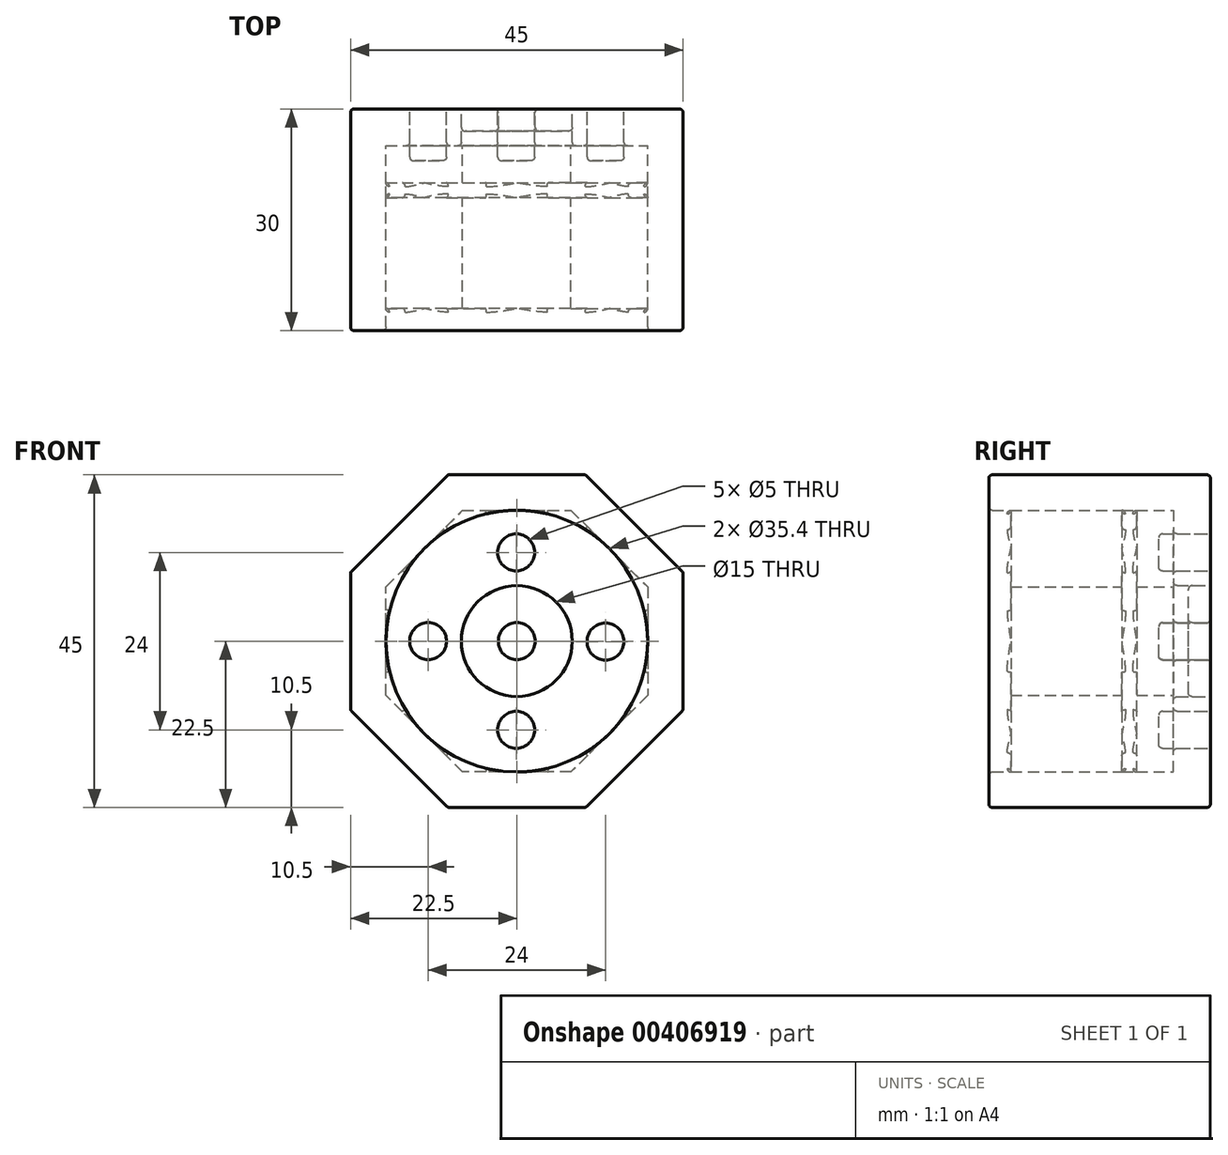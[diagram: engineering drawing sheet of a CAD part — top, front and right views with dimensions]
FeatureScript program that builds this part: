
annotation { "Feature Type Name" : "Feature", "Feature Type Description" : "" }
export const myFeature = defineFeature(function(context is Context, id is Id, definition is map)
    precondition{}
    {
        {
            var Q0;
            Q0=qCreatedBy(makeId("Front.planeOp"),FACE);
            var sketch = newSketch(context, id + "F0", { "sketchPlane" : qUnion([Q0])});
            skCircle(sketch, "E0.cCircle", {"center": v(0, 0) * mm, "radius": 17.7 * mm, "construction": true});
            skLineSegment(sketch, "E0.0", {"start": v(17.7, 7.33) * mm, "end": v(17.7, -7.33) * mm});
            skLineSegment(sketch, "E0.1", {"start": v(17.7, -7.33) * mm, "end": v(7.33, -17.7) * mm});
            skLineSegment(sketch, "E0.2", {"start": v(7.33, -17.7) * mm, "end": v(-7.33, -17.7) * mm});
            skLineSegment(sketch, "E0.3", {"start": v(-7.33, -17.7) * mm, "end": v(-17.7, -7.33) * mm});
            skLineSegment(sketch, "E0.4", {"start": v(-17.7, -7.33) * mm, "end": v(-17.7, 7.33) * mm});
            skLineSegment(sketch, "E0.5", {"start": v(-17.7, 7.33) * mm, "end": v(-7.33, 17.7) * mm});
            skLineSegment(sketch, "E0.6", {"start": v(-7.33, 17.7) * mm, "end": v(7.33, 17.7) * mm});
            skLineSegment(sketch, "E0.7", {"start": v(7.33, 17.7) * mm, "end": v(17.7, 7.33) * mm});
            skPoint(sketch, "E0.0.midPoint", {"position": v(17.7, 0) * mm});
            skCircle(sketch, "E1.cCircle", {"center": v(0, 0) * mm, "radius": 22.5 * mm, "construction": true});
            skLineSegment(sketch, "E1.0", {"start": v(9.32, 22.5) * mm, "end": v(22.5, 9.32) * mm});
            skLineSegment(sketch, "E1.1", {"start": v(22.5, 9.32) * mm, "end": v(22.5, -9.32) * mm});
            skLineSegment(sketch, "E1.2", {"start": v(22.5, -9.32) * mm, "end": v(9.32, -22.5) * mm});
            skLineSegment(sketch, "E1.3", {"start": v(9.32, -22.5) * mm, "end": v(-9.32, -22.5) * mm});
            skLineSegment(sketch, "E1.4", {"start": v(-9.32, -22.5) * mm, "end": v(-22.5, -9.32) * mm});
            skLineSegment(sketch, "E1.5", {"start": v(-22.5, -9.32) * mm, "end": v(-22.5, 9.32) * mm});
            skLineSegment(sketch, "E1.6", {"start": v(-22.5, 9.32) * mm, "end": v(-9.32, 22.5) * mm});
            skLineSegment(sketch, "E1.7", {"start": v(-9.32, 22.5) * mm, "end": v(9.32, 22.5) * mm});
            skPoint(sketch, "E1.0.midPoint", {"position": v(15.9, 15.9) * mm});
            skCircle(sketch, "E2", {"center": v(0, 0) * mm, "radius": 2.5 * mm});
            skCircle(sketch, "E3", {"center": v(0, 0) * mm, "radius": 7.5 * mm});
            skCircle(sketch, "E4", {"center": v(-12, 0) * mm, "radius": 2.5 * mm});
            skCircle(sketch, "E5", {"center": v(-0.08, 12) * mm, "radius": 2.5 * mm});
            skCircle(sketch, "E6", {"center": v(12, -0.06) * mm, "radius": 2.5 * mm});
            skCircle(sketch, "E7", {"center": v(-0.08, -12) * mm, "radius": 2.5 * mm});
            skSolve(sketch);
        }
        {
            var Q0;
            Q0=makeQuery(id+"F0.imprint","IMPRINT",FACE,{"disambiguationData":[TD([[makeQuery(id+"F0.imprint","IMPRINT",EDGE,{"derivedFrom":sQuery(id+"F0.wireOp",EDGE,"E2")}),-1.0]])]});
            extrude(context, id + "F1", {"entities" : qUnion([Q0]), "depth" : 3 * mm});
        }
        {
            var Q0;
            Q0=makeQuery(id+"F0.imprint","IMPRINT",FACE,{"disambiguationData":[TD([[makeQuery(id+"F0.imprint","IMPRINT",EDGE,{"derivedFrom":sQuery(id+"F0.wireOp",EDGE,"E4")}),1.0]])]});
            var Q1;
            Q1=makeQuery(id+"F0.imprint","IMPRINT",FACE,{"disambiguationData":[TD([[makeQuery(id+"F0.imprint","IMPRINT",EDGE,{"derivedFrom":sQuery(id+"F0.wireOp",EDGE,"E5")}),1.0]])]});
            var Q2;
            Q2=makeQuery(id+"F0.imprint","IMPRINT",FACE,{"disambiguationData":[TD([[makeQuery(id+"F0.imprint","IMPRINT",EDGE,{"derivedFrom":sQuery(id+"F0.wireOp",EDGE,"E6")}),1.0]])]});
            var Q3;
            Q3=makeQuery(id+"F0.imprint","IMPRINT",FACE,{"disambiguationData":[TD([[makeQuery(id+"F0.imprint","IMPRINT",EDGE,{"derivedFrom":sQuery(id+"F0.wireOp",EDGE,"E7")}),1.0]])]});
            extrude(context, id + "F2", {"entities" : qUnion([Q0, Q1, Q2, Q3]), "depth" : 7 * mm});
        }
        {
            var Q0;
            Q0=makeQuery(id+"F0.imprint","IMPRINT",FACE,{"disambiguationData":[TD([[makeQuery(id+"F0.imprint","IMPRINT",EDGE,{"derivedFrom":sQuery(id+"F0.wireOp",EDGE,"E0.0")}),-1.0]])]});
            extrude(context, id + "F3", {"entities" : qUnion([Q0]), "depth" : 5 * mm});
        }
        {
            var Q0;
            Q0=makeQuery(id+"F0.imprint","IMPRINT",FACE,{"disambiguationData":[TD([[makeQuery(id+"F0.imprint","IMPRINT",EDGE,{"derivedFrom":sQuery(id+"F0.wireOp",EDGE,"E0.0")}),1.0]])]});
            extrude(context, id + "F4", {"entities" : qUnion([Q0]), "operationType" : NewBodyOperationType.ADD, "depth" : 10 * mm});
        }
        {
            var Q0;
            Q0=makeQuery(id+"F4.opExtrude","CAP_FACE",FACE,{"disambiguationData":[OSD([sQuery(id+"F0.wireOp",EDGE,"E0.0"),sQuery(id+"F0.wireOp",EDGE,"E0.1"),sQuery(id+"F0.wireOp",EDGE,"E0.2"),sQuery(id+"F0.wireOp",EDGE,"E0.3"),sQuery(id+"F0.wireOp",EDGE,"E0.4"),sQuery(id+"F0.wireOp",EDGE,"E0.5"),sQuery(id+"F0.wireOp",EDGE,"E0.6"),sQuery(id+"F0.wireOp",EDGE,"E0.7"),sQuery(id+"F0.wireOp",EDGE,"E1.0"),sQuery(id+"F0.wireOp",EDGE,"E1.1"),sQuery(id+"F0.wireOp",EDGE,"E1.2"),sQuery(id+"F0.wireOp",EDGE,"E1.3"),sQuery(id+"F0.wireOp",EDGE,"E1.4"),sQuery(id+"F0.wireOp",EDGE,"E1.5"),sQuery(id+"F0.wireOp",EDGE,"E1.6"),sQuery(id+"F0.wireOp",EDGE,"E1.7")])],"isStart":false});
            var sketch = newSketch(context, id + "F5", { "sketchPlane" : qUnion([Q0])});
            skCircle(sketch, "E8", {"center": v(0, 0) * mm, "radius": 17.7 * mm});
            skSolve(sketch);
        }
        {
            var Q0;
            {var subQ0=sQuery(id+"F5.wireOp",EDGE,"E8");var subQ1=makeQuery(id+"F4.opExtrude","CAP_EDGE",EDGE,{"disambiguationData":[OSD([sQuery(id+"F0.wireOp",EDGE,"E0.4")])],"isStart":false});var subQ2=makeQuery(id+"F5.imprint","INTERSECT",VERTEX,{"derivedFrom":[subQ1,subQ0]});Q0=makeQuery(id+"F5.imprint","IMPRINT",FACE,{"disambiguationData":[TD([[makeQuery(id+"F5.imprint","IMPRINT",EDGE,{"disambiguationData":[TD([[subQ2,-1.0]])],"derivedFrom":subQ0}),-1.0]])]});}
            var Q1;
            {var subQ0=sQuery(id+"F5.wireOp",EDGE,"E8");var subQ1=makeQuery(id+"F4.opExtrude","CAP_EDGE",EDGE,{"disambiguationData":[OSD([sQuery(id+"F0.wireOp",EDGE,"E0.5")])],"isStart":false});var subQ2=makeQuery(id+"F5.imprint","INTERSECT",VERTEX,{"derivedFrom":[subQ1,subQ0]});Q1=makeQuery(id+"F5.imprint","IMPRINT",FACE,{"disambiguationData":[TD([[makeQuery(id+"F5.imprint","IMPRINT",EDGE,{"disambiguationData":[TD([[subQ2,-1.0]])],"derivedFrom":subQ0}),-1.0]])]});}
            var Q2;
            {var subQ0=sQuery(id+"F5.wireOp",EDGE,"E8");var subQ1=makeQuery(id+"F4.opExtrude","CAP_EDGE",EDGE,{"disambiguationData":[OSD([sQuery(id+"F0.wireOp",EDGE,"E0.6")])],"isStart":false});var subQ2=makeQuery(id+"F5.imprint","INTERSECT",VERTEX,{"derivedFrom":[subQ1,subQ0]});Q2=makeQuery(id+"F5.imprint","IMPRINT",FACE,{"disambiguationData":[TD([[makeQuery(id+"F5.imprint","IMPRINT",EDGE,{"disambiguationData":[TD([[subQ2,-1.0]])],"derivedFrom":subQ0}),-1.0]])]});}
            var Q3;
            {var subQ0=sQuery(id+"F5.wireOp",EDGE,"E8");var subQ1=makeQuery(id+"F4.opExtrude","CAP_EDGE",EDGE,{"disambiguationData":[OSD([sQuery(id+"F0.wireOp",EDGE,"E0.7")])],"isStart":false});var subQ2=makeQuery(id+"F5.imprint","INTERSECT",VERTEX,{"derivedFrom":[subQ1,subQ0]});Q3=makeQuery(id+"F5.imprint","IMPRINT",FACE,{"disambiguationData":[TD([[makeQuery(id+"F5.imprint","IMPRINT",EDGE,{"disambiguationData":[TD([[subQ2,-1.0]])],"derivedFrom":subQ0}),-1.0]])]});}
            var Q4;
            {var subQ0=sQuery(id+"F5.wireOp",EDGE,"E8");var subQ1=makeQuery(id+"F4.opExtrude","CAP_EDGE",EDGE,{"disambiguationData":[OSD([sQuery(id+"F0.wireOp",EDGE,"E0.7")])],"isStart":false});var subQ2=makeQuery(id+"F5.imprint","INTERSECT",VERTEX,{"derivedFrom":[subQ1,subQ0]});Q4=makeQuery(id+"F5.imprint","IMPRINT",FACE,{"disambiguationData":[TD([[makeQuery(id+"F5.imprint","IMPRINT",EDGE,{"disambiguationData":[TD([[subQ2,1.0]])],"derivedFrom":subQ0}),-1.0]])]});}
            var Q5;
            {var subQ0=sQuery(id+"F5.wireOp",EDGE,"E8");var subQ1=makeQuery(id+"F4.opExtrude","CAP_EDGE",EDGE,{"disambiguationData":[OSD([sQuery(id+"F0.wireOp",EDGE,"E0.0")])],"isStart":false});var subQ2=makeQuery(id+"F5.imprint","INTERSECT",VERTEX,{"derivedFrom":[subQ1,subQ0]});Q5=makeQuery(id+"F5.imprint","IMPRINT",FACE,{"disambiguationData":[TD([[makeQuery(id+"F5.imprint","IMPRINT",EDGE,{"disambiguationData":[TD([[subQ2,1.0]])],"derivedFrom":subQ0}),-1.0]])]});}
            var Q6;
            {var subQ0=sQuery(id+"F5.wireOp",EDGE,"E8");var subQ1=makeQuery(id+"F4.opExtrude","CAP_EDGE",EDGE,{"disambiguationData":[OSD([sQuery(id+"F0.wireOp",EDGE,"E0.2")])],"isStart":false});var subQ2=makeQuery(id+"F5.imprint","INTERSECT",VERTEX,{"derivedFrom":[subQ1,subQ0]});Q6=makeQuery(id+"F5.imprint","IMPRINT",FACE,{"disambiguationData":[TD([[makeQuery(id+"F5.imprint","IMPRINT",EDGE,{"disambiguationData":[TD([[subQ2,-1.0]])],"derivedFrom":subQ0}),-1.0]])]});}
            var Q7;
            {var subQ0=sQuery(id+"F5.wireOp",EDGE,"E8");var subQ1=makeQuery(id+"F4.opExtrude","CAP_EDGE",EDGE,{"disambiguationData":[OSD([sQuery(id+"F0.wireOp",EDGE,"E0.3")])],"isStart":false});var subQ2=makeQuery(id+"F5.imprint","INTERSECT",VERTEX,{"derivedFrom":[subQ1,subQ0]});Q7=makeQuery(id+"F5.imprint","IMPRINT",FACE,{"disambiguationData":[TD([[makeQuery(id+"F5.imprint","IMPRINT",EDGE,{"disambiguationData":[TD([[subQ2,-1.0]])],"derivedFrom":subQ0}),-1.0]])]});}
            var Q8;
            Q8=makeQuery(id+"F5.imprint","IMPRINT",FACE,{"disambiguationData":[TD([[makeQuery(id+"F5.imprint","IMPRINT",EDGE,{"derivedFrom":makeQuery(id+"F4.opExtrude","CAP_EDGE",EDGE,{"disambiguationData":[OSD([sQuery(id+"F0.wireOp",EDGE,"E1.0")])],"isStart":false})}),-1.0]])]});
            extrude(context, id + "F6", {"entities" : qUnion([Q0, Q1, Q2, Q3, Q4, Q5, Q6, Q7, Q8]), "operationType" : NewBodyOperationType.ADD, "depth" : 2 * mm});
        }
        {
            var Q0;
            Q0=makeQuery(id+"F6.opExtrude","CAP_FACE",FACE,{"disambiguationData":[OSD([sQuery(id+"F0.wireOp",EDGE,"E1.0"),sQuery(id+"F0.wireOp",EDGE,"E1.1"),sQuery(id+"F0.wireOp",EDGE,"E1.2"),sQuery(id+"F0.wireOp",EDGE,"E1.3"),sQuery(id+"F0.wireOp",EDGE,"E1.4"),sQuery(id+"F0.wireOp",EDGE,"E1.5"),sQuery(id+"F0.wireOp",EDGE,"E1.6"),sQuery(id+"F0.wireOp",EDGE,"E1.7"),sQuery(id+"F5.wireOp",EDGE,"E8")])],"isStart":false});
            var sketch = newSketch(context, id + "F7", { "sketchPlane" : qUnion([Q0])});
            skCircle(sketch, "E9.cCircle", {"center": v(0, 0) * mm, "radius": 17.7 * mm, "construction": true});
            skLineSegment(sketch, "E10.0", {"start": v(-17.7, -7.33) * mm, "end": v(-17.7, 7.33) * mm});
            skLineSegment(sketch, "E10.1", {"start": v(-17.7, 7.33) * mm, "end": v(-7.33, 17.7) * mm});
            skLineSegment(sketch, "E10.2", {"start": v(-7.33, 17.7) * mm, "end": v(7.33, 17.7) * mm});
            skLineSegment(sketch, "E10.3", {"start": v(7.33, 17.7) * mm, "end": v(17.7, 7.33) * mm});
            skLineSegment(sketch, "E10.4", {"start": v(17.7, 7.33) * mm, "end": v(17.7, -7.33) * mm});
            skLineSegment(sketch, "E10.5", {"start": v(17.7, -7.33) * mm, "end": v(7.33, -17.7) * mm});
            skLineSegment(sketch, "E10.6", {"start": v(7.33, -17.7) * mm, "end": v(-7.33, -17.7) * mm});
            skLineSegment(sketch, "E10.7", {"start": v(-7.33, -17.7) * mm, "end": v(-17.7, -7.33) * mm});
            skPoint(sketch, "E10.0.midPoint", {"position": v(-17.7, 0) * mm});
            skSolve(sketch);
        }
        {
            var Q0;
            Q0=makeQuery(id+"F7.imprint","IMPRINT",FACE,{"disambiguationData":[TD([[makeQuery(id+"F7.imprint","IMPRINT",EDGE,{"derivedFrom":makeQuery(id+"F6.opExtrude","CAP_EDGE",EDGE,{"disambiguationData":[OSD([sQuery(id+"F0.wireOp",EDGE,"E1.0")])],"isStart":false})}),-1.0]])]});
            extrude(context, id + "F8", {"entities" : qUnion([Q0]), "operationType" : NewBodyOperationType.ADD, "depth" : 15 * mm});
        }
        {
            var Q0;
            Q0=makeQuery(id+"F8.opExtrude","CAP_FACE",FACE,{"disambiguationData":[OSD([sQuery(id+"F0.wireOp",EDGE,"E1.0"),sQuery(id+"F0.wireOp",EDGE,"E1.1"),sQuery(id+"F0.wireOp",EDGE,"E1.2"),sQuery(id+"F0.wireOp",EDGE,"E1.3"),sQuery(id+"F0.wireOp",EDGE,"E1.4"),sQuery(id+"F0.wireOp",EDGE,"E1.5"),sQuery(id+"F0.wireOp",EDGE,"E1.6"),sQuery(id+"F0.wireOp",EDGE,"E1.7"),sQuery(id+"F7.wireOp",EDGE,"E9.0"),sQuery(id+"F7.wireOp",EDGE,"E9.1"),sQuery(id+"F7.wireOp",EDGE,"E9.2"),sQuery(id+"F7.wireOp",EDGE,"E9.3"),sQuery(id+"F7.wireOp",EDGE,"E9.4"),sQuery(id+"F7.wireOp",EDGE,"E9.5"),sQuery(id+"F7.wireOp",EDGE,"E9.6"),sQuery(id+"F7.wireOp",EDGE,"E9.7"),sQuery(id+"F7.wireOp",EDGE,"E9.8")])],"isStart":false});
            var sketch = newSketch(context, id + "F9", { "sketchPlane" : qUnion([Q0])});
            skCircle(sketch, "E11", {"center": v(0, 0) * mm, "radius": 17.7 * mm});
            skSolve(sketch);
        }
        {
            var Q0;
            {var subQ0=sQuery(id+"F9.wireOp",EDGE,"E11");var subQ1=makeQuery(id+"F8.opExtrude","CAP_EDGE",EDGE,{"disambiguationData":[OSD([sQuery(id+"F7.wireOp",EDGE,"E9.5")])],"isStart":false});var subQ2=makeQuery(id+"F9.imprint","INTERSECT",VERTEX,{"derivedFrom":[subQ1,subQ0]});Q0=makeQuery(id+"F9.imprint","IMPRINT",FACE,{"disambiguationData":[TD([[makeQuery(id+"F9.imprint","IMPRINT",EDGE,{"disambiguationData":[TD([[subQ2,-1.0]])],"derivedFrom":subQ0}),-1.0]])]});}
            var Q1;
            {var subQ0=sQuery(id+"F9.wireOp",EDGE,"E11");var subQ1=makeQuery(id+"F8.opExtrude","CAP_EDGE",EDGE,{"disambiguationData":[OSD([sQuery(id+"F7.wireOp",EDGE,"E9.6")])],"isStart":false});var subQ2=makeQuery(id+"F9.imprint","INTERSECT",VERTEX,{"derivedFrom":[subQ1,subQ0]});Q1=makeQuery(id+"F9.imprint","IMPRINT",FACE,{"disambiguationData":[TD([[makeQuery(id+"F9.imprint","IMPRINT",EDGE,{"disambiguationData":[TD([[subQ2,-1.0]])],"derivedFrom":subQ0}),-1.0]])]});}
            var Q2;
            {var subQ0=sQuery(id+"F9.wireOp",EDGE,"E11");var subQ1=makeQuery(id+"F8.opExtrude","CAP_EDGE",EDGE,{"disambiguationData":[OSD([sQuery(id+"F7.wireOp",EDGE,"E9.7")])],"isStart":false});var subQ2=makeQuery(id+"F9.imprint","INTERSECT",VERTEX,{"derivedFrom":[subQ1,subQ0]});Q2=makeQuery(id+"F9.imprint","IMPRINT",FACE,{"disambiguationData":[TD([[makeQuery(id+"F9.imprint","IMPRINT",EDGE,{"disambiguationData":[TD([[subQ2,-1.0]])],"derivedFrom":subQ0}),-1.0]])]});}
            var Q3;
            {var subQ0=sQuery(id+"F9.wireOp",EDGE,"E11");var subQ1=makeQuery(id+"F8.opExtrude","CAP_EDGE",EDGE,{"disambiguationData":[OSD([sQuery(id+"F7.wireOp",EDGE,"E9.8")])],"isStart":false});var subQ2=makeQuery(id+"F9.imprint","INTERSECT",VERTEX,{"derivedFrom":[subQ1,subQ0]});Q3=makeQuery(id+"F9.imprint","IMPRINT",FACE,{"disambiguationData":[TD([[makeQuery(id+"F9.imprint","IMPRINT",EDGE,{"disambiguationData":[TD([[subQ2,-1.0]])],"derivedFrom":subQ0}),-1.0]])]});}
            var Q4;
            {var subQ0=sQuery(id+"F9.wireOp",EDGE,"E11");var subQ1=makeQuery(id+"F8.opExtrude","CAP_EDGE",EDGE,{"disambiguationData":[OSD([sQuery(id+"F7.wireOp",EDGE,"E9.0")])],"isStart":false});var subQ2=makeQuery(id+"F9.imprint","INTERSECT",VERTEX,{"derivedFrom":[subQ1,subQ0]});Q4=makeQuery(id+"F9.imprint","IMPRINT",FACE,{"disambiguationData":[TD([[makeQuery(id+"F9.imprint","IMPRINT",EDGE,{"disambiguationData":[TD([[subQ2,-1.0]])],"derivedFrom":subQ0}),-1.0]])]});}
            var Q5;
            {var subQ0=sQuery(id+"F9.wireOp",EDGE,"E11");var subQ1=makeQuery(id+"F8.opExtrude","CAP_EDGE",EDGE,{"disambiguationData":[OSD([sQuery(id+"F7.wireOp",EDGE,"E9.0")])],"isStart":false});var subQ2=makeQuery(id+"F9.imprint","INTERSECT",VERTEX,{"derivedFrom":[subQ1,subQ0]});Q5=makeQuery(id+"F9.imprint","IMPRINT",FACE,{"disambiguationData":[TD([[makeQuery(id+"F9.imprint","IMPRINT",EDGE,{"disambiguationData":[TD([[subQ2,1.0]])],"derivedFrom":subQ0}),-1.0]])]});}
            var Q6;
            {var subQ0=sQuery(id+"F9.wireOp",EDGE,"E11");var subQ1=makeQuery(id+"F8.opExtrude","CAP_EDGE",EDGE,{"disambiguationData":[OSD([sQuery(id+"F7.wireOp",EDGE,"E9.1")])],"isStart":false});var subQ2=makeQuery(id+"F9.imprint","INTERSECT",VERTEX,{"derivedFrom":[subQ1,subQ0]});Q6=makeQuery(id+"F9.imprint","IMPRINT",FACE,{"disambiguationData":[TD([[makeQuery(id+"F9.imprint","IMPRINT",EDGE,{"disambiguationData":[TD([[subQ2,1.0]])],"derivedFrom":subQ0}),-1.0]])]});}
            var Q7;
            {var subQ0=sQuery(id+"F9.wireOp",EDGE,"E11");var subQ1=makeQuery(id+"F8.opExtrude","CAP_EDGE",EDGE,{"disambiguationData":[OSD([sQuery(id+"F7.wireOp",EDGE,"E9.3")])],"isStart":false});var subQ2=makeQuery(id+"F9.imprint","INTERSECT",VERTEX,{"derivedFrom":[subQ1,subQ0]});Q7=makeQuery(id+"F9.imprint","IMPRINT",FACE,{"disambiguationData":[TD([[makeQuery(id+"F9.imprint","IMPRINT",EDGE,{"disambiguationData":[TD([[subQ2,-1.0]])],"derivedFrom":subQ0}),-1.0]])]});}
            var Q8;
            {var subQ0=sQuery(id+"F9.wireOp",EDGE,"E11");var subQ1=makeQuery(id+"F8.opExtrude","CAP_EDGE",EDGE,{"disambiguationData":[OSD([sQuery(id+"F7.wireOp",EDGE,"E9.4")])],"isStart":false});var subQ2=makeQuery(id+"F9.imprint","INTERSECT",VERTEX,{"derivedFrom":[subQ1,subQ0]});Q8=makeQuery(id+"F9.imprint","IMPRINT",FACE,{"disambiguationData":[TD([[makeQuery(id+"F9.imprint","IMPRINT",EDGE,{"disambiguationData":[TD([[subQ2,-1.0]])],"derivedFrom":subQ0}),-1.0]])]});}
            var Q9;
            Q9=makeQuery(id+"F9.imprint","IMPRINT",FACE,{"disambiguationData":[TD([[makeQuery(id+"F9.imprint","IMPRINT",EDGE,{"derivedFrom":makeQuery(id+"F8.opExtrude","CAP_EDGE",EDGE,{"disambiguationData":[OSD([sQuery(id+"F0.wireOp",EDGE,"E1.0")])],"isStart":false})}),-1.0]])]});
            extrude(context, id + "F10", {"entities" : qUnion([Q0, Q1, Q2, Q3, Q4, Q5, Q6, Q7, Q8, Q9]), "operationType" : NewBodyOperationType.ADD, "depth" : 3 * mm});
        }
        {
            var Q0;
            Q0=makeQuery(id+"F1.opExtrude","CAP_EDGE",EDGE,{"disambiguationData":[OSD([sQuery(id+"F0.wireOp",EDGE,"E2")])],"isStart":true});
            var Q1;
            Q1=makeQuery(id+"F4.opExtrude","CAP_EDGE",EDGE,{"disambiguationData":[OSD([sQuery(id+"F0.wireOp",EDGE,"E1.7")])],"isStart":true});
            var Q2;
            Q2=makeQuery(id+"F4.opExtrude","CAP_EDGE",EDGE,{"disambiguationData":[OSD([sQuery(id+"F0.wireOp",EDGE,"E1.6")])],"isStart":true});
            var Q3;
            Q3=makeQuery(id+"F4.opExtrude","CAP_EDGE",EDGE,{"disambiguationData":[OSD([sQuery(id+"F0.wireOp",EDGE,"E1.5")])],"isStart":true});
            var Q4;
            Q4=makeQuery(id+"F4.opExtrude","CAP_EDGE",EDGE,{"disambiguationData":[OSD([sQuery(id+"F0.wireOp",EDGE,"E1.4")])],"isStart":true});
            var Q5;
            Q5=makeQuery(id+"F4.opExtrude","CAP_EDGE",EDGE,{"disambiguationData":[OSD([sQuery(id+"F0.wireOp",EDGE,"E1.3")])],"isStart":true});
            var Q6;
            Q6=makeQuery(id+"F4.opExtrude","CAP_EDGE",EDGE,{"disambiguationData":[OSD([sQuery(id+"F0.wireOp",EDGE,"E1.2")])],"isStart":true});
            var Q7;
            Q7=makeQuery(id+"F4.opExtrude","CAP_EDGE",EDGE,{"disambiguationData":[OSD([sQuery(id+"F0.wireOp",EDGE,"E1.1")])],"isStart":true});
            var Q8;
            Q8=makeQuery(id+"F4.opExtrude","CAP_EDGE",EDGE,{"disambiguationData":[OSD([sQuery(id+"F0.wireOp",EDGE,"E1.0")])],"isStart":true});
            var Q9;
            {var subQ0=sQuery(id+"F0.wireOp",EDGE,"E1.6");Q9=makeQuery(id+"F10.boolean.opBoolean","MERGE",FACE,{"derivedFrom":[makeQuery(id+"F8.boolean.opBoolean","MERGE",FACE,{"derivedFrom":[makeQuery(id+"F6.boolean.opBoolean","MERGE",FACE,{"derivedFrom":[makeQuery(id+"F4.opExtrude","SWEPT_FACE",FACE,{"disambiguationData":[OSD([subQ0])]}),makeQuery(id+"F6.opExtrude","SWEPT_FACE",FACE,{"disambiguationData":[OSD([subQ0])]})]}),makeQuery(id+"F8.opExtrude","SWEPT_FACE",FACE,{"disambiguationData":[OSD([subQ0])]})]}),makeQuery(id+"F10.opExtrude","SWEPT_FACE",FACE,{"disambiguationData":[OSD([subQ0])]})]});}
            var Q10;
            {var subQ0=sQuery(id+"F0.wireOp",EDGE,"E1.5");Q10=makeQuery(id+"F10.boolean.opBoolean","MERGE",FACE,{"derivedFrom":[makeQuery(id+"F8.boolean.opBoolean","MERGE",FACE,{"derivedFrom":[makeQuery(id+"F6.boolean.opBoolean","MERGE",FACE,{"derivedFrom":[makeQuery(id+"F4.opExtrude","SWEPT_FACE",FACE,{"disambiguationData":[OSD([subQ0])]}),makeQuery(id+"F6.opExtrude","SWEPT_FACE",FACE,{"disambiguationData":[OSD([subQ0])]})]}),makeQuery(id+"F8.opExtrude","SWEPT_FACE",FACE,{"disambiguationData":[OSD([subQ0])]})]}),makeQuery(id+"F10.opExtrude","SWEPT_FACE",FACE,{"disambiguationData":[OSD([subQ0])]})]});}
            var Q11;
            {var subQ0=sQuery(id+"F0.wireOp",EDGE,"E1.4");Q11=makeQuery(id+"F10.boolean.opBoolean","MERGE",FACE,{"derivedFrom":[makeQuery(id+"F8.boolean.opBoolean","MERGE",FACE,{"derivedFrom":[makeQuery(id+"F6.boolean.opBoolean","MERGE",FACE,{"derivedFrom":[makeQuery(id+"F4.opExtrude","SWEPT_FACE",FACE,{"disambiguationData":[OSD([subQ0])]}),makeQuery(id+"F6.opExtrude","SWEPT_FACE",FACE,{"disambiguationData":[OSD([subQ0])]})]}),makeQuery(id+"F8.opExtrude","SWEPT_FACE",FACE,{"disambiguationData":[OSD([subQ0])]})]}),makeQuery(id+"F10.opExtrude","SWEPT_FACE",FACE,{"disambiguationData":[OSD([subQ0])]})]});}
            var Q12;
            {var subQ0=sQuery(id+"F0.wireOp",EDGE,"E1.7");Q12=makeQuery(id+"F10.boolean.opBoolean","MERGE",FACE,{"derivedFrom":[makeQuery(id+"F8.boolean.opBoolean","MERGE",FACE,{"derivedFrom":[makeQuery(id+"F6.boolean.opBoolean","MERGE",FACE,{"derivedFrom":[makeQuery(id+"F4.opExtrude","SWEPT_FACE",FACE,{"disambiguationData":[OSD([subQ0])]}),makeQuery(id+"F6.opExtrude","SWEPT_FACE",FACE,{"disambiguationData":[OSD([subQ0])]})]}),makeQuery(id+"F8.opExtrude","SWEPT_FACE",FACE,{"disambiguationData":[OSD([subQ0])]})]}),makeQuery(id+"F10.opExtrude","SWEPT_FACE",FACE,{"disambiguationData":[OSD([subQ0])]})]});}
            var Q13;
            {var subQ0=sQuery(id+"F0.wireOp",EDGE,"E1.0");Q13=makeQuery(id+"F10.boolean.opBoolean","MERGE",FACE,{"derivedFrom":[makeQuery(id+"F8.boolean.opBoolean","MERGE",FACE,{"derivedFrom":[makeQuery(id+"F6.boolean.opBoolean","MERGE",FACE,{"derivedFrom":[makeQuery(id+"F4.opExtrude","SWEPT_FACE",FACE,{"disambiguationData":[OSD([subQ0])]}),makeQuery(id+"F6.opExtrude","SWEPT_FACE",FACE,{"disambiguationData":[OSD([subQ0])]})]}),makeQuery(id+"F8.opExtrude","SWEPT_FACE",FACE,{"disambiguationData":[OSD([subQ0])]})]}),makeQuery(id+"F10.opExtrude","SWEPT_FACE",FACE,{"disambiguationData":[OSD([subQ0])]})]});}
            var Q14;
            {var subQ0=sQuery(id+"F0.wireOp",EDGE,"E1.1");Q14=makeQuery(id+"F10.boolean.opBoolean","MERGE",FACE,{"derivedFrom":[makeQuery(id+"F8.boolean.opBoolean","MERGE",FACE,{"derivedFrom":[makeQuery(id+"F6.boolean.opBoolean","MERGE",FACE,{"derivedFrom":[makeQuery(id+"F4.opExtrude","SWEPT_FACE",FACE,{"disambiguationData":[OSD([subQ0])]}),makeQuery(id+"F6.opExtrude","SWEPT_FACE",FACE,{"disambiguationData":[OSD([subQ0])]})]}),makeQuery(id+"F8.opExtrude","SWEPT_FACE",FACE,{"disambiguationData":[OSD([subQ0])]})]}),makeQuery(id+"F10.opExtrude","SWEPT_FACE",FACE,{"disambiguationData":[OSD([subQ0])]})]});}
            var Q15;
            {var subQ0=sQuery(id+"F0.wireOp",EDGE,"E1.2");Q15=makeQuery(id+"F10.boolean.opBoolean","MERGE",FACE,{"derivedFrom":[makeQuery(id+"F8.boolean.opBoolean","MERGE",FACE,{"derivedFrom":[makeQuery(id+"F6.boolean.opBoolean","MERGE",FACE,{"derivedFrom":[makeQuery(id+"F4.opExtrude","SWEPT_FACE",FACE,{"disambiguationData":[OSD([subQ0])]}),makeQuery(id+"F6.opExtrude","SWEPT_FACE",FACE,{"disambiguationData":[OSD([subQ0])]})]}),makeQuery(id+"F8.opExtrude","SWEPT_FACE",FACE,{"disambiguationData":[OSD([subQ0])]})]}),makeQuery(id+"F10.opExtrude","SWEPT_FACE",FACE,{"disambiguationData":[OSD([subQ0])]})]});}
            var Q16;
            {var subQ0=sQuery(id+"F0.wireOp",EDGE,"E1.3");Q16=makeQuery(id+"F10.boolean.opBoolean","MERGE",FACE,{"derivedFrom":[makeQuery(id+"F8.boolean.opBoolean","MERGE",FACE,{"derivedFrom":[makeQuery(id+"F6.boolean.opBoolean","MERGE",FACE,{"derivedFrom":[makeQuery(id+"F4.opExtrude","SWEPT_FACE",FACE,{"disambiguationData":[OSD([subQ0])]}),makeQuery(id+"F6.opExtrude","SWEPT_FACE",FACE,{"disambiguationData":[OSD([subQ0])]})]}),makeQuery(id+"F8.opExtrude","SWEPT_FACE",FACE,{"disambiguationData":[OSD([subQ0])]})]}),makeQuery(id+"F10.opExtrude","SWEPT_FACE",FACE,{"disambiguationData":[OSD([subQ0])]})]});}
            var Q17;
            Q17=makeQuery(id+"F2.opExtrude","CAP_EDGE",EDGE,{"disambiguationData":[OSD([sQuery(id+"F0.wireOp",EDGE,"E7")])],"isStart":false});
            var Q18;
            Q18=makeQuery(id+"F2.opExtrude","CAP_EDGE",EDGE,{"disambiguationData":[OSD([sQuery(id+"F0.wireOp",EDGE,"E4")])],"isStart":false});
            var Q19;
            Q19=makeQuery(id+"F3.opExtrude","CAP_EDGE",EDGE,{"disambiguationData":[OSD([sQuery(id+"F0.wireOp",EDGE,"E3")])],"isStart":false});
            var Q20;
            Q20=makeQuery(id+"F1.opExtrude","CAP_EDGE",EDGE,{"disambiguationData":[OSD([sQuery(id+"F0.wireOp",EDGE,"E3")])],"isStart":false});
            var Q21;
            Q21=makeQuery(id+"F1.opExtrude","CAP_EDGE",EDGE,{"disambiguationData":[OSD([sQuery(id+"F0.wireOp",EDGE,"E2")])],"isStart":false});
            var Q22;
            Q22=makeQuery(id+"F2.opExtrude","CAP_EDGE",EDGE,{"disambiguationData":[OSD([sQuery(id+"F0.wireOp",EDGE,"E6")])],"isStart":false});
            var Q23;
            Q23=makeQuery(id+"F2.opExtrude","CAP_EDGE",EDGE,{"disambiguationData":[OSD([sQuery(id+"F0.wireOp",EDGE,"E5")])],"isStart":false});
            var Q24;
            Q24=makeQuery(id+"F3.opExtrude","CAP_EDGE",EDGE,{"disambiguationData":[OSD([sQuery(id+"F0.wireOp",EDGE,"E7")])],"isStart":false});
            var Q25;
            Q25=makeQuery(id+"F3.opExtrude","CAP_EDGE",EDGE,{"disambiguationData":[OSD([sQuery(id+"F0.wireOp",EDGE,"E6")])],"isStart":false});
            var Q26;
            Q26=makeQuery(id+"F3.opExtrude","CAP_EDGE",EDGE,{"disambiguationData":[OSD([sQuery(id+"F0.wireOp",EDGE,"E5")])],"isStart":false});
            var Q27;
            Q27=makeQuery(id+"F3.opExtrude","CAP_EDGE",EDGE,{"disambiguationData":[OSD([sQuery(id+"F0.wireOp",EDGE,"E4")])],"isStart":false});
            var Q28;
            Q28=makeQuery(id+"F10.opExtrude","CAP_EDGE",EDGE,{"disambiguationData":[OSD([sQuery(id+"F9.wireOp",EDGE,"E11")])],"isStart":false});
            var Q29;
            {var subQ0=sQuery(id+"F9.wireOp",EDGE,"E11");Q29=makeQuery(id+"F10.boolean.opBoolean","SPLIT",EDGE,{"disambiguationData":[TD([makeQuery(id+"F8.opExtrude","SWEPT_FACE",FACE,{"disambiguationData":[OSD([sQuery(id+"F7.wireOp",EDGE,"E9.3")])]}),makeQuery(id+"F8.opExtrude","SWEPT_FACE",FACE,{"disambiguationData":[OSD([sQuery(id+"F7.wireOp",EDGE,"E9.4")])]}),makeQuery(id+"F10.opExtrude","SWEPT_FACE",FACE,{"disambiguationData":[OSD([subQ0])]}),makeQuery(id+"F10.opExtrude","CAP_FACE",FACE,{"disambiguationData":[OSD([sQuery(id+"F0.wireOp",EDGE,"E1.0"),sQuery(id+"F0.wireOp",EDGE,"E1.1"),sQuery(id+"F0.wireOp",EDGE,"E1.2"),sQuery(id+"F0.wireOp",EDGE,"E1.3"),sQuery(id+"F0.wireOp",EDGE,"E1.4"),sQuery(id+"F0.wireOp",EDGE,"E1.5"),sQuery(id+"F0.wireOp",EDGE,"E1.6"),sQuery(id+"F0.wireOp",EDGE,"E1.7"),subQ0])],"isStart":true})])],"derivedFrom":makeQuery(id+"F10.opExtrude","CAP_EDGE",EDGE,{"disambiguationData":[OSD([subQ0])],"isStart":true})});}
            var Q30;
            {var subQ0=sQuery(id+"F9.wireOp",EDGE,"E11");Q30=makeQuery(id+"F10.boolean.opBoolean","SPLIT",EDGE,{"disambiguationData":[TD([makeQuery(id+"F8.opExtrude","SWEPT_FACE",FACE,{"disambiguationData":[OSD([sQuery(id+"F7.wireOp",EDGE,"E9.4")])]}),makeQuery(id+"F8.opExtrude","SWEPT_FACE",FACE,{"disambiguationData":[OSD([sQuery(id+"F7.wireOp",EDGE,"E9.5")])]}),makeQuery(id+"F10.opExtrude","SWEPT_FACE",FACE,{"disambiguationData":[OSD([subQ0])]}),makeQuery(id+"F10.opExtrude","CAP_FACE",FACE,{"disambiguationData":[OSD([sQuery(id+"F0.wireOp",EDGE,"E1.0"),sQuery(id+"F0.wireOp",EDGE,"E1.1"),sQuery(id+"F0.wireOp",EDGE,"E1.2"),sQuery(id+"F0.wireOp",EDGE,"E1.3"),sQuery(id+"F0.wireOp",EDGE,"E1.4"),sQuery(id+"F0.wireOp",EDGE,"E1.5"),sQuery(id+"F0.wireOp",EDGE,"E1.6"),sQuery(id+"F0.wireOp",EDGE,"E1.7"),subQ0])],"isStart":true})])],"derivedFrom":makeQuery(id+"F10.opExtrude","CAP_EDGE",EDGE,{"disambiguationData":[OSD([subQ0])],"isStart":true})});}
            var Q31;
            {var subQ0=sQuery(id+"F9.wireOp",EDGE,"E11");Q31=makeQuery(id+"F10.boolean.opBoolean","SPLIT",EDGE,{"disambiguationData":[TD([makeQuery(id+"F8.opExtrude","SWEPT_FACE",FACE,{"disambiguationData":[OSD([sQuery(id+"F7.wireOp",EDGE,"E9.5")])]}),makeQuery(id+"F8.opExtrude","SWEPT_FACE",FACE,{"disambiguationData":[OSD([sQuery(id+"F7.wireOp",EDGE,"E9.6")])]}),makeQuery(id+"F10.opExtrude","SWEPT_FACE",FACE,{"disambiguationData":[OSD([subQ0])]}),makeQuery(id+"F10.opExtrude","CAP_FACE",FACE,{"disambiguationData":[OSD([sQuery(id+"F0.wireOp",EDGE,"E1.0"),sQuery(id+"F0.wireOp",EDGE,"E1.1"),sQuery(id+"F0.wireOp",EDGE,"E1.2"),sQuery(id+"F0.wireOp",EDGE,"E1.3"),sQuery(id+"F0.wireOp",EDGE,"E1.4"),sQuery(id+"F0.wireOp",EDGE,"E1.5"),sQuery(id+"F0.wireOp",EDGE,"E1.6"),sQuery(id+"F0.wireOp",EDGE,"E1.7"),subQ0])],"isStart":true})])],"derivedFrom":makeQuery(id+"F10.opExtrude","CAP_EDGE",EDGE,{"disambiguationData":[OSD([subQ0])],"isStart":true})});}
            var Q32;
            {var subQ0=sQuery(id+"F9.wireOp",EDGE,"E11");Q32=makeQuery(id+"F10.boolean.opBoolean","SPLIT",EDGE,{"disambiguationData":[TD([makeQuery(id+"F8.opExtrude","SWEPT_FACE",FACE,{"disambiguationData":[OSD([sQuery(id+"F7.wireOp",EDGE,"E9.2")])]}),makeQuery(id+"F8.opExtrude","SWEPT_FACE",FACE,{"disambiguationData":[OSD([sQuery(id+"F7.wireOp",EDGE,"E9.3")])]}),makeQuery(id+"F10.opExtrude","SWEPT_FACE",FACE,{"disambiguationData":[OSD([subQ0])]}),makeQuery(id+"F10.opExtrude","CAP_FACE",FACE,{"disambiguationData":[OSD([sQuery(id+"F0.wireOp",EDGE,"E1.0"),sQuery(id+"F0.wireOp",EDGE,"E1.1"),sQuery(id+"F0.wireOp",EDGE,"E1.2"),sQuery(id+"F0.wireOp",EDGE,"E1.3"),sQuery(id+"F0.wireOp",EDGE,"E1.4"),sQuery(id+"F0.wireOp",EDGE,"E1.5"),sQuery(id+"F0.wireOp",EDGE,"E1.6"),sQuery(id+"F0.wireOp",EDGE,"E1.7"),subQ0])],"isStart":true})])],"derivedFrom":makeQuery(id+"F10.opExtrude","CAP_EDGE",EDGE,{"disambiguationData":[OSD([subQ0])],"isStart":true})});}
            var Q33;
            {var subQ0=sQuery(id+"F9.wireOp",EDGE,"E11");Q33=makeQuery(id+"F10.boolean.opBoolean","SPLIT",EDGE,{"disambiguationData":[TD([makeQuery(id+"F8.opExtrude","SWEPT_FACE",FACE,{"disambiguationData":[OSD([sQuery(id+"F7.wireOp",EDGE,"E9.1")])]}),makeQuery(id+"F8.opExtrude","SWEPT_FACE",FACE,{"disambiguationData":[OSD([sQuery(id+"F7.wireOp",EDGE,"E9.2")])]}),makeQuery(id+"F10.opExtrude","SWEPT_FACE",FACE,{"disambiguationData":[OSD([subQ0])]}),makeQuery(id+"F10.opExtrude","CAP_FACE",FACE,{"disambiguationData":[OSD([sQuery(id+"F0.wireOp",EDGE,"E1.0"),sQuery(id+"F0.wireOp",EDGE,"E1.1"),sQuery(id+"F0.wireOp",EDGE,"E1.2"),sQuery(id+"F0.wireOp",EDGE,"E1.3"),sQuery(id+"F0.wireOp",EDGE,"E1.4"),sQuery(id+"F0.wireOp",EDGE,"E1.5"),sQuery(id+"F0.wireOp",EDGE,"E1.6"),sQuery(id+"F0.wireOp",EDGE,"E1.7"),subQ0])],"isStart":true})])],"derivedFrom":makeQuery(id+"F10.opExtrude","CAP_EDGE",EDGE,{"disambiguationData":[OSD([subQ0])],"isStart":true})});}
            var Q34;
            {var subQ0=sQuery(id+"F9.wireOp",EDGE,"E11");Q34=makeQuery(id+"F10.boolean.opBoolean","SPLIT",EDGE,{"disambiguationData":[TD([makeQuery(id+"F8.opExtrude","SWEPT_FACE",FACE,{"disambiguationData":[OSD([sQuery(id+"F7.wireOp",EDGE,"E9.0")])]}),makeQuery(id+"F8.opExtrude","SWEPT_FACE",FACE,{"disambiguationData":[OSD([sQuery(id+"F7.wireOp",EDGE,"E9.1")])]}),makeQuery(id+"F10.opExtrude","SWEPT_FACE",FACE,{"disambiguationData":[OSD([subQ0])]}),makeQuery(id+"F10.opExtrude","CAP_FACE",FACE,{"disambiguationData":[OSD([sQuery(id+"F0.wireOp",EDGE,"E1.0"),sQuery(id+"F0.wireOp",EDGE,"E1.1"),sQuery(id+"F0.wireOp",EDGE,"E1.2"),sQuery(id+"F0.wireOp",EDGE,"E1.3"),sQuery(id+"F0.wireOp",EDGE,"E1.4"),sQuery(id+"F0.wireOp",EDGE,"E1.5"),sQuery(id+"F0.wireOp",EDGE,"E1.6"),sQuery(id+"F0.wireOp",EDGE,"E1.7"),subQ0])],"isStart":true})])],"derivedFrom":makeQuery(id+"F10.opExtrude","CAP_EDGE",EDGE,{"disambiguationData":[OSD([subQ0])],"isStart":true})});}
            var Q35;
            {var subQ0=sQuery(id+"F9.wireOp",EDGE,"E11");Q35=makeQuery(id+"F10.boolean.opBoolean","SPLIT",EDGE,{"disambiguationData":[TD([makeQuery(id+"F8.opExtrude","SWEPT_FACE",FACE,{"disambiguationData":[OSD([sQuery(id+"F7.wireOp",EDGE,"E9.0")])]}),makeQuery(id+"F8.opExtrude","SWEPT_FACE",FACE,{"disambiguationData":[OSD([sQuery(id+"F7.wireOp",EDGE,"E9.8")])]}),makeQuery(id+"F10.opExtrude","SWEPT_FACE",FACE,{"disambiguationData":[OSD([subQ0])]}),makeQuery(id+"F10.opExtrude","CAP_FACE",FACE,{"disambiguationData":[OSD([sQuery(id+"F0.wireOp",EDGE,"E1.0"),sQuery(id+"F0.wireOp",EDGE,"E1.1"),sQuery(id+"F0.wireOp",EDGE,"E1.2"),sQuery(id+"F0.wireOp",EDGE,"E1.3"),sQuery(id+"F0.wireOp",EDGE,"E1.4"),sQuery(id+"F0.wireOp",EDGE,"E1.5"),sQuery(id+"F0.wireOp",EDGE,"E1.6"),sQuery(id+"F0.wireOp",EDGE,"E1.7"),subQ0])],"isStart":true})])],"derivedFrom":makeQuery(id+"F10.opExtrude","CAP_EDGE",EDGE,{"disambiguationData":[OSD([subQ0])],"isStart":true})});}
            var Q36;
            {var subQ0=sQuery(id+"F9.wireOp",EDGE,"E11");Q36=makeQuery(id+"F10.boolean.opBoolean","SPLIT",EDGE,{"disambiguationData":[TD([makeQuery(id+"F8.opExtrude","SWEPT_FACE",FACE,{"disambiguationData":[OSD([sQuery(id+"F7.wireOp",EDGE,"E9.6")])]}),makeQuery(id+"F8.opExtrude","SWEPT_FACE",FACE,{"disambiguationData":[OSD([sQuery(id+"F7.wireOp",EDGE,"E9.7")])]}),makeQuery(id+"F10.opExtrude","SWEPT_FACE",FACE,{"disambiguationData":[OSD([subQ0])]}),makeQuery(id+"F10.opExtrude","CAP_FACE",FACE,{"disambiguationData":[OSD([sQuery(id+"F0.wireOp",EDGE,"E1.0"),sQuery(id+"F0.wireOp",EDGE,"E1.1"),sQuery(id+"F0.wireOp",EDGE,"E1.2"),sQuery(id+"F0.wireOp",EDGE,"E1.3"),sQuery(id+"F0.wireOp",EDGE,"E1.4"),sQuery(id+"F0.wireOp",EDGE,"E1.5"),sQuery(id+"F0.wireOp",EDGE,"E1.6"),sQuery(id+"F0.wireOp",EDGE,"E1.7"),subQ0])],"isStart":true})])],"derivedFrom":makeQuery(id+"F10.opExtrude","CAP_EDGE",EDGE,{"disambiguationData":[OSD([subQ0])],"isStart":true})});}
            var Q37;
            {var subQ0=sQuery(id+"F9.wireOp",EDGE,"E11");Q37=makeQuery(id+"F10.boolean.opBoolean","SPLIT",EDGE,{"disambiguationData":[TD([makeQuery(id+"F8.opExtrude","SWEPT_FACE",FACE,{"disambiguationData":[OSD([sQuery(id+"F7.wireOp",EDGE,"E9.7")])]}),makeQuery(id+"F8.opExtrude","SWEPT_FACE",FACE,{"disambiguationData":[OSD([sQuery(id+"F7.wireOp",EDGE,"E9.8")])]}),makeQuery(id+"F10.opExtrude","SWEPT_FACE",FACE,{"disambiguationData":[OSD([subQ0])]}),makeQuery(id+"F10.opExtrude","CAP_FACE",FACE,{"disambiguationData":[OSD([sQuery(id+"F0.wireOp",EDGE,"E1.0"),sQuery(id+"F0.wireOp",EDGE,"E1.1"),sQuery(id+"F0.wireOp",EDGE,"E1.2"),sQuery(id+"F0.wireOp",EDGE,"E1.3"),sQuery(id+"F0.wireOp",EDGE,"E1.4"),sQuery(id+"F0.wireOp",EDGE,"E1.5"),sQuery(id+"F0.wireOp",EDGE,"E1.6"),sQuery(id+"F0.wireOp",EDGE,"E1.7"),subQ0])],"isStart":true})])],"derivedFrom":makeQuery(id+"F10.opExtrude","CAP_EDGE",EDGE,{"disambiguationData":[OSD([subQ0])],"isStart":true})});}
            var Q38;
            {var subQ0=sQuery(id+"F5.wireOp",EDGE,"E8");Q38=makeQuery(id+"F8.boolean.opBoolean","SPLIT",EDGE,{"disambiguationData":[TD([makeQuery(id+"F6.opExtrude","SWEPT_FACE",FACE,{"disambiguationData":[OSD([subQ0])]}),makeQuery(id+"F6.opExtrude","CAP_FACE",FACE,{"disambiguationData":[OSD([sQuery(id+"F0.wireOp",EDGE,"E1.0"),sQuery(id+"F0.wireOp",EDGE,"E1.1"),sQuery(id+"F0.wireOp",EDGE,"E1.2"),sQuery(id+"F0.wireOp",EDGE,"E1.3"),sQuery(id+"F0.wireOp",EDGE,"E1.4"),sQuery(id+"F0.wireOp",EDGE,"E1.5"),sQuery(id+"F0.wireOp",EDGE,"E1.6"),sQuery(id+"F0.wireOp",EDGE,"E1.7"),subQ0])],"isStart":false}),makeQuery(id+"F8.opExtrude","SWEPT_FACE",FACE,{"disambiguationData":[OSD([sQuery(id+"F7.wireOp",EDGE,"E9.3")])]}),makeQuery(id+"F8.opExtrude","SWEPT_FACE",FACE,{"disambiguationData":[OSD([sQuery(id+"F7.wireOp",EDGE,"E9.4")])]})])],"derivedFrom":makeQuery(id+"F6.opExtrude","CAP_EDGE",EDGE,{"disambiguationData":[OSD([subQ0])],"isStart":false})});}
            var Q39;
            {var subQ0=sQuery(id+"F5.wireOp",EDGE,"E8");Q39=makeQuery(id+"F8.boolean.opBoolean","SPLIT",EDGE,{"disambiguationData":[TD([makeQuery(id+"F6.opExtrude","SWEPT_FACE",FACE,{"disambiguationData":[OSD([subQ0])]}),makeQuery(id+"F6.opExtrude","CAP_FACE",FACE,{"disambiguationData":[OSD([sQuery(id+"F0.wireOp",EDGE,"E1.0"),sQuery(id+"F0.wireOp",EDGE,"E1.1"),sQuery(id+"F0.wireOp",EDGE,"E1.2"),sQuery(id+"F0.wireOp",EDGE,"E1.3"),sQuery(id+"F0.wireOp",EDGE,"E1.4"),sQuery(id+"F0.wireOp",EDGE,"E1.5"),sQuery(id+"F0.wireOp",EDGE,"E1.6"),sQuery(id+"F0.wireOp",EDGE,"E1.7"),subQ0])],"isStart":false}),makeQuery(id+"F8.opExtrude","SWEPT_FACE",FACE,{"disambiguationData":[OSD([sQuery(id+"F7.wireOp",EDGE,"E9.2")])]}),makeQuery(id+"F8.opExtrude","SWEPT_FACE",FACE,{"disambiguationData":[OSD([sQuery(id+"F7.wireOp",EDGE,"E9.3")])]})])],"derivedFrom":makeQuery(id+"F6.opExtrude","CAP_EDGE",EDGE,{"disambiguationData":[OSD([subQ0])],"isStart":false})});}
            var Q40;
            {var subQ0=sQuery(id+"F5.wireOp",EDGE,"E8");Q40=makeQuery(id+"F8.boolean.opBoolean","SPLIT",EDGE,{"disambiguationData":[TD([makeQuery(id+"F6.opExtrude","SWEPT_FACE",FACE,{"disambiguationData":[OSD([subQ0])]}),makeQuery(id+"F6.opExtrude","CAP_FACE",FACE,{"disambiguationData":[OSD([sQuery(id+"F0.wireOp",EDGE,"E1.0"),sQuery(id+"F0.wireOp",EDGE,"E1.1"),sQuery(id+"F0.wireOp",EDGE,"E1.2"),sQuery(id+"F0.wireOp",EDGE,"E1.3"),sQuery(id+"F0.wireOp",EDGE,"E1.4"),sQuery(id+"F0.wireOp",EDGE,"E1.5"),sQuery(id+"F0.wireOp",EDGE,"E1.6"),sQuery(id+"F0.wireOp",EDGE,"E1.7"),subQ0])],"isStart":false}),makeQuery(id+"F8.opExtrude","SWEPT_FACE",FACE,{"disambiguationData":[OSD([sQuery(id+"F7.wireOp",EDGE,"E9.4")])]}),makeQuery(id+"F8.opExtrude","SWEPT_FACE",FACE,{"disambiguationData":[OSD([sQuery(id+"F7.wireOp",EDGE,"E9.5")])]})])],"derivedFrom":makeQuery(id+"F6.opExtrude","CAP_EDGE",EDGE,{"disambiguationData":[OSD([subQ0])],"isStart":false})});}
            var Q41;
            Q41=makeQuery(id+"F6.opExtrude","SWEPT_FACE",FACE,{"disambiguationData":[OSD([sQuery(id+"F5.wireOp",EDGE,"E8")])]});
            fillet(context, id + "F11", {"entities" : qUnion([Q0, Q1, Q2, Q3, Q4, Q5, Q6, Q7, Q8, Q9, Q10, Q11, Q12, Q13, Q14, Q15, Q16, Q17, Q18, Q19, Q20, Q21, Q22, Q23, Q24, Q25, Q26, Q27, Q28, Q29, Q30, Q31, Q32, Q33, Q34, Q35, Q36, Q37, Q38, Q39, Q40, Q41]), "radius" : 0.5 * mm, "tangentPropagation" : true, "allowEdgeOverflow" : false});
        }
    });
